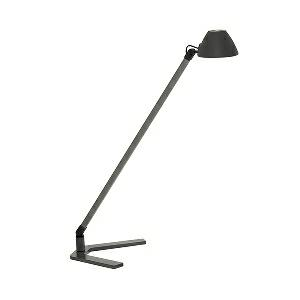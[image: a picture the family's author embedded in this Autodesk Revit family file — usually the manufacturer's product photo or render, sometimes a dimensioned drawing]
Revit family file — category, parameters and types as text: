
# Revit family: lucio_-_lum_500_840_d_00804142_5ae1
name_source: partatom
category: Lighting Fixtures
units: mm (PartAtom-declared; Revit-internal decimal feet)

## family parameters
Cut with Voids When Loaded = No
Host = Face
Light Source = No
Part Type = Normal
Room Calculation Point = No
Round Connector Dimension = Use Diameter
Shared = No

## types (1)
- LUCIO - LUM 500/840/D (1 x LED, 300 lm, 4000K)
    Apparent Load = 4 VA
    Approval mark = CE
    CIE Flux Codes = 84 97 99 100 100
    Color Rendering = 80-89
    Color Temperature = 4000K
    Control Gear = Electronic ballast
    Default Elevation = 1800 mm
    Description = LUM 500/840/D|Task luminaire|light source: LED module|work equipment: Electronic plug-in transformer|connected load: 100-240 V, 50/60 Hz|Power consumption: approx. 4 W|standby: approx. 0,30|power factor: approx. 0,970|luminous flux: 300 lm|luminous efficacy: 75 lm/W|Illuminance efficiency factor: 0 lx/W|colour temperature: Cold white, ca. 4000 K|color rendering index (CRI): >= 80|chromaticity tolerance:  3 SDCM|class of protection: II with plug-in power supply, III without plug-in power supply|technology: Continuously dimmable|luminaire body|material: Plastic|surface: Untreated|colour: Umbra grey|lamp cover: Polycarbonate (PC), Satine|tubular sections|material: Tubular aluminium section|surface: Anodized|Form: Tubular section upright|colour: Titanium|weight (net): approx. 1.0 kg|mains lead: 1.85 m Mains plug CEE 7/XVI|Fastening: Adaptor (accessory), Table base, Table clamp (accessory)|glare control: Optics|special features: Push button in luminaire head|Approval mark: VDE - ENEC|
    Frequency = 50 Hz
    Height = 55 mm
    Lamp = 1 x LED
    Lamp Light Flux = 300 lm
    Lamp count = 1
    Length = 90 mm
    Luminous efficacy = 75 lm/W
    Manufacturer = Waldmann
    ModVariant = No
    Model = 00804142
    Mounting Place = Table
    Mounting Type = Surface mounted
    Number of Poles = 1
    OnlyDefault = Yes
    Power Factor = 1
    Product Name = LUCIO - LUM 500/840/D
    Product group = Task luminaire (office)
    ProductGroupID = 21
    Protection Class = Protection class II
    Protection Degree = IP 20
    RLX_Detail_Level = 1
    RLX_Emergency_Light_Flux = 0 lm
    RLX_Emergency_Type = 0
    RLX_Emergency_Type_DB = No
    RlxData = <blob elided: 63197 chars, md5=d2ae1880>
    Socket = socket
    Standby Power = 0 W
    System Light Flux = 300 lm
    System Power = 4 W
    Type Comments = Product without accessories
    Type Image = 00804142.jpg
    URL = http://relux.com
    VarID = ---
    Voltage = 230 V
    Voltage Range = 220-240 V
    Weight = 0.00 kg
    Width = 0 mm  [stored 0 ft]

note: [stored X ft] marks values corroborated as IEEE doubles in the binary element streams (Revit-internal decimal feet)

## geometry (parser evidence)
native form markers: Blend x4, Sweep x15
no freeform markers — native parametric forms only
